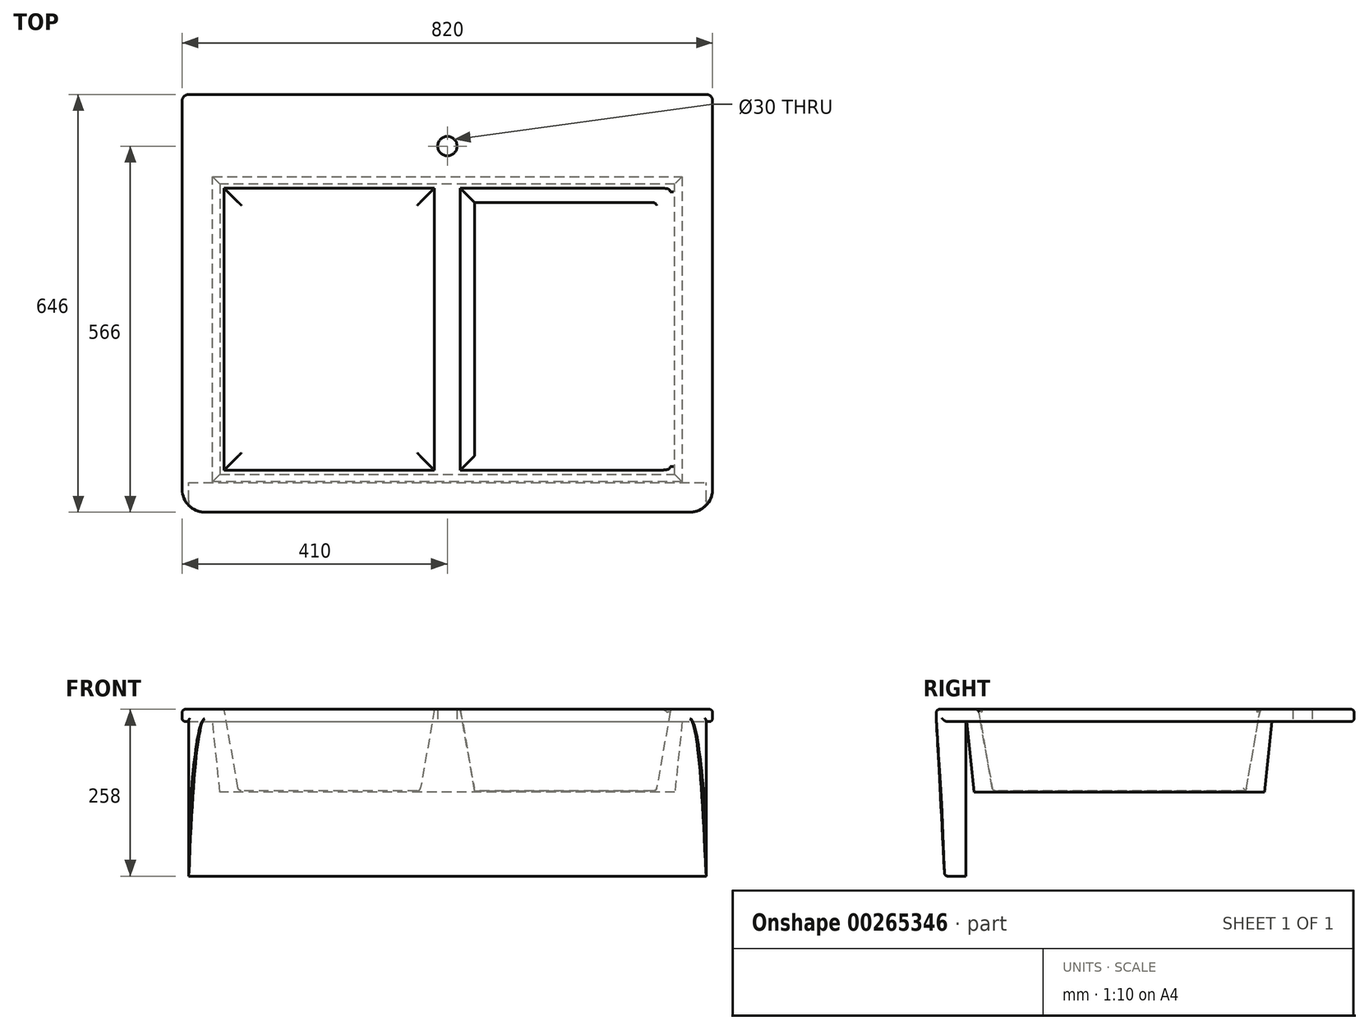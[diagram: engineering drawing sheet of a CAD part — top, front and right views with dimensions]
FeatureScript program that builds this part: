
annotation { "Feature Type Name" : "Feature", "Feature Type Description" : "" }
export const myFeature = defineFeature(function(context is Context, id is Id, definition is map)
    precondition{}
    {
        {
            var Q0;
            Q0=qCreatedBy(makeId("Top.planeOp"),FACE);
            var sketch = newSketch(context, id + "F0", { "sketchPlane" : qUnion([Q0])});
            skLineSegment(sketch, "E0.bottom", {"start": v(-400, 323) * mm, "end": v(400, 323) * mm});
            skLineSegment(sketch, "E0.top", {"start": v(-375, -323) * mm, "end": v(375, -323) * mm});
            skLineSegment(sketch, "E0.left", {"start": v(-410, 313) * mm, "end": v(-410, -288) * mm});
            skLineSegment(sketch, "E0.right", {"start": v(410, 313) * mm, "end": v(410, -288) * mm});
            skPoint(sketch, "E0.middle", {"position": v(0, 0) * mm});
            skPoint(sketch, "E1.visualSharp", {"position": v(-410, 323) * mm});
            skArc(sketch, "E1.filletArc", {"start": v(-400, 323) * mm, "mid": v(-407.07, 320.07) * mm, "end": v(-410, 313) * mm});
            skPoint(sketch, "E2.MirrorP", {"position": v(0, 646) * mm});
            skArc(sketch, "E3.MirrorCS", {"start": v(400, 323) * mm, "mid": v(407.07, 320.07) * mm, "end": v(410, 313) * mm});
            skPoint(sketch, "E4.orphan", {"position": v(410, 323) * mm});
            skPoint(sketch, "E5.visualSharp", {"position": v(410, -323) * mm});
            skArc(sketch, "E5.filletArc", {"start": v(375, -323) * mm, "mid": v(399.75, -312.75) * mm, "end": v(410, -288) * mm});
            skArc(sketch, "E6.MirrorCS", {"start": v(-375, -323) * mm, "mid": v(-399.75, -312.75) * mm, "end": v(-410, -288) * mm});
            skPoint(sketch, "E7.orphan", {"position": v(-410, -323) * mm});
            skLineSegment(sketch, "E8.bottom", {"start": v(20, -258) * mm, "end": v(345, -258) * mm});
            skLineSegment(sketch, "E8.top", {"start": v(20, 178) * mm, "end": v(345, 178) * mm});
            skLineSegment(sketch, "E8.left", {"start": v(20, -258) * mm, "end": v(20, 178) * mm});
            skLineSegment(sketch, "E8.right", {"start": v(345, -258) * mm, "end": v(345, 178) * mm});
            skPoint(sketch, "E8.middle", {"position": v(182.5, -40) * mm});
            skLineSegment(sketch, "E9.MirrorCS", {"start": v(-20, -258) * mm, "end": v(-345, -258) * mm});
            skLineSegment(sketch, "E10.MirrorCS", {"start": v(-20, 178) * mm, "end": v(-345, 178) * mm});
            skLineSegment(sketch, "E11.MirrorCS", {"start": v(-20, -258) * mm, "end": v(-20, 178) * mm});
            skLineSegment(sketch, "E12.MirrorCS", {"start": v(-345, -258) * mm, "end": v(-345, 178) * mm});
            skCircle(sketch, "E13", {"center": v(0, 243) * mm, "radius": 15 * mm});
            skLineSegment(sketch, "E14.0", {"start": v(0, 198) * mm, "end": v(-365, 198) * mm});
            skLineSegment(sketch, "E14.1", {"start": v(0, -278) * mm, "end": v(0, 198) * mm});
            skLineSegment(sketch, "E14.2", {"start": v(0, -278) * mm, "end": v(-365, -278) * mm});
            skLineSegment(sketch, "E14.3", {"start": v(-365, -278) * mm, "end": v(-365, 198) * mm});
            skLineSegment(sketch, "E15.MirrorCS", {"start": v(0, -278) * mm, "end": v(365, -278) * mm});
            skLineSegment(sketch, "E16.MirrorCS", {"start": v(0, 198) * mm, "end": v(365, 198) * mm});
            skLineSegment(sketch, "E17.MirrorCS", {"start": v(365, -278) * mm, "end": v(365, 198) * mm});
            skSolve(sketch);
        }
        {
            var Q0;
            Q0=makeQuery(id+"F0.imprint","IMPRINT",FACE,{"disambiguationData":[TD([[makeQuery(id+"F0.imprint","IMPRINT",EDGE,{"derivedFrom":sQuery(id+"F0.wireOp",EDGE,"E9.MirrorCS")}),-1.0]])]});
            var Q1;
            Q1=makeQuery(id+"F0.imprint","IMPRINT",FACE,{"disambiguationData":[TD([[makeQuery(id+"F0.imprint","IMPRINT",EDGE,{"derivedFrom":sQuery(id+"F0.wireOp",EDGE,"E13")}),1.0]])]});
            var Q2;
            Q2=makeQuery(id+"F0.imprint","IMPRINT",FACE,{"disambiguationData":[TD([[makeQuery(id+"F0.imprint","IMPRINT",EDGE,{"derivedFrom":sQuery(id+"F0.wireOp",EDGE,"E8.bottom")}),1.0]])]});
            var Q3;
            Q3=makeQuery(id+"F0.imprint","IMPRINT",FACE,{"disambiguationData":[TD([[makeQuery(id+"F0.imprint","IMPRINT",EDGE,{"derivedFrom":sQuery(id+"F0.wireOp",EDGE,"E9.MirrorCS")}),1.0]])]});
            var Q4;
            Q4=makeQuery(id+"F0.imprint","IMPRINT",FACE,{"disambiguationData":[TD([[makeQuery(id+"F0.imprint","IMPRINT",EDGE,{"derivedFrom":sQuery(id+"F0.wireOp",EDGE,"E8.bottom")}),-1.0]])]});
            var Q5;
            Q5=makeQuery(id+"F0.imprint","IMPRINT",FACE,{"disambiguationData":[TD([[makeQuery(id+"F0.imprint","IMPRINT",EDGE,{"derivedFrom":sQuery(id+"F0.wireOp",EDGE,"E0.bottom")}),-1.0]])]});
            extrude(context, id + "F1", {"entities" : qUnion([Q0, Q1, Q2, Q3, Q4, Q5]), "oppositeDirection" : true, "depth" : 258 * mm});
        }
        {
            var Q0;
            Q0=makeQuery(id+"F1.opExtrude","SWEPT_FACE",FACE,{"disambiguationData":[OSD([sQuery(id+"F0.wireOp",EDGE,"E0.right")])]});
            var sketch = newSketch(context, id + "F2", { "sketchPlane" : qUnion([Q0])});
            skLineSegment(sketch, "E18.bottom", {"start": v(-277, -258) * mm, "end": v(323, -258) * mm});
            skLineSegment(sketch, "E18.top", {"start": v(-277, -19) * mm, "end": v(323, -19) * mm});
            skLineSegment(sketch, "E18.left", {"start": v(-277, -258) * mm, "end": v(-277, -19) * mm});
            skLineSegment(sketch, "E18.right", {"start": v(323, -258) * mm, "end": v(323, -19) * mm});
            skSolve(sketch);
        }
        {
            var Q0;
            Q0 = qSketchRegion(id + "F2", true);
            extrude(context, id + "F3", {"entities" : qUnion([Q0]), "operationType" : NewBodyOperationType.REMOVE, "oppositeDirection" : true, "depth" : 820 * mm});
        }
        {
            var Q0;
            Q0=makeQuery(id+"F0.imprint","IMPRINT",FACE,{"disambiguationData":[TD([[makeQuery(id+"F0.imprint","IMPRINT",EDGE,{"derivedFrom":sQuery(id+"F0.wireOp",EDGE,"E8.bottom")}),-1.0]])]});
            var Q1;
            Q1=makeQuery(id+"F0.imprint","IMPRINT",FACE,{"disambiguationData":[TD([[makeQuery(id+"F0.imprint","IMPRINT",EDGE,{"derivedFrom":sQuery(id+"F0.wireOp",EDGE,"E9.MirrorCS")}),1.0]])]});
            var Q2;
            Q2=makeQuery(id+"F0.imprint","IMPRINT",FACE,{"disambiguationData":[TD([[makeQuery(id+"F0.imprint","IMPRINT",EDGE,{"derivedFrom":sQuery(id+"F0.wireOp",EDGE,"E8.bottom")}),1.0]])]});
            var Q3;
            Q3=makeQuery(id+"F0.imprint","IMPRINT",FACE,{"disambiguationData":[TD([[makeQuery(id+"F0.imprint","IMPRINT",EDGE,{"derivedFrom":sQuery(id+"F0.wireOp",EDGE,"E9.MirrorCS")}),-1.0]])]});
            extrude(context, id + "F4", {"entities" : qUnion([Q0, Q1, Q2, Q3]), "operationType" : NewBodyOperationType.ADD, "oppositeDirection" : true, "depth" : 128 * mm, "hasDraft" : true, "draftAngle" : 6 * degree, "draftPullDirection" : true});
        }
        {
            var Q0;
            Q0=makeQuery(id+"F0.imprint","IMPRINT",FACE,{"disambiguationData":[TD([[makeQuery(id+"F0.imprint","IMPRINT",EDGE,{"derivedFrom":sQuery(id+"F0.wireOp",EDGE,"E8.bottom")}),1.0]])]});
            var Q1;
            Q1=makeQuery(id+"F0.imprint","IMPRINT",FACE,{"disambiguationData":[TD([[makeQuery(id+"F0.imprint","IMPRINT",EDGE,{"derivedFrom":sQuery(id+"F0.wireOp",EDGE,"E9.MirrorCS")}),-1.0]])]});
            extrude(context, id + "F5", {"entities" : qUnion([Q0, Q1]), "operationType" : NewBodyOperationType.REMOVE, "oppositeDirection" : true, "depth" : 126 * mm, "hasDraft" : true, "draftAngle" : 10 * degree, "draftPullDirection" : true});
        }
        {
            var Q0;
            Q0=sQuery(id+"F0.wireOp",VERTEX,"E13.center");
            var Q1;
            Q1=makeQuery(id+"F1.opExtrude","SWEPT_BODY",BODY,{"disambiguationData":[OSD([sQuery(id+"F0.wireOp",EDGE,"E0.bottom"),sQuery(id+"F0.wireOp",EDGE,"E0.top"),sQuery(id+"F0.wireOp",EDGE,"E0.left"),sQuery(id+"F0.wireOp",EDGE,"E0.right"),sQuery(id+"F0.wireOp",EDGE,"E1.filletArc"),sQuery(id+"F0.wireOp",EDGE,"E3.MirrorCS"),sQuery(id+"F0.wireOp",EDGE,"E5.filletArc"),sQuery(id+"F0.wireOp",EDGE,"E6.MirrorCS")])]});
            hole(context, id + "F6", {"style" : HoleStyle.SIMPLE, "endStyle" : HoleEndStyle.THROUGH, "holeDiameter" : 30 * mm, "tappedDepth" : 12 * mm, "tapClearance" : 3, "locations" : qUnion([Q0]), "scope" : qUnion([Q1]), "startStyle" : HoleStartStyle.PART});
        }
        {
            var Q0;
            Q0=makeQuery(id+"F1.opExtrude","SWEPT_FACE",FACE,{"disambiguationData":[OSD([sQuery(id+"F0.wireOp",EDGE,"E0.right")])]});
            var sketch = newSketch(context, id + "F7", { "sketchPlane" : qUnion([Q0])});
            skLineSegment(sketch, "E19", {"start": v(-323.78, 0) * mm, "end": v(-309.6, -267.77) * mm});
            skLineSegment(sketch, "E20", {"start": v(-309.6, -267.77) * mm, "end": v(-332.86, -267.77) * mm});
            skLineSegment(sketch, "E21", {"start": v(-332.86, -267.77) * mm, "end": v(-323.78, 0) * mm});
            skSolve(sketch);
        }
        {
            var Q0;
            Q0 = qSketchRegion(id + "F7", true);
            extrude(context, id + "F8", {"entities" : qUnion([Q0]), "operationType" : NewBodyOperationType.REMOVE, "oppositeDirection" : true, "depth" : 820 * mm});
        }
        {
            var Q0;
            Q0=makeQuery(id+"F1.opExtrude","CAP_EDGE",EDGE,{"disambiguationData":[OSD([sQuery(id+"F0.wireOp",EDGE,"E0.top")])],"isStart":true});
            var Q1;
            Q1=makeQuery(id+"F5.boolean.opBoolean","COPY",EDGE,{"derivedFrom":makeQuery(id+"F5.opExtrude","CAP_EDGE",EDGE,{"disambiguationData":[OSD([sQuery(id+"F0.wireOp",EDGE,"E10.MirrorCS")])],"isStart":true})});
            var Q2;
            Q2=makeQuery(id+"F5.boolean.opBoolean","COPY",EDGE,{"derivedFrom":makeQuery(id+"F5.opExtrude","CAP_EDGE",EDGE,{"disambiguationData":[OSD([sQuery(id+"F0.wireOp",EDGE,"E12.MirrorCS")])],"isStart":true})});
            var Q3;
            Q3=makeQuery(id+"F5.boolean.opBoolean","COPY",EDGE,{"derivedFrom":makeQuery(id+"F5.opExtrude","CAP_EDGE",EDGE,{"disambiguationData":[OSD([sQuery(id+"F0.wireOp",EDGE,"E9.MirrorCS")])],"isStart":true})});
            var Q4;
            Q4=makeQuery(id+"F5.boolean.opBoolean","COPY",EDGE,{"derivedFrom":makeQuery(id+"F5.opExtrude","CAP_EDGE",EDGE,{"disambiguationData":[OSD([sQuery(id+"F0.wireOp",EDGE,"E11.MirrorCS")])],"isStart":true})});
            var Q5;
            Q5=makeQuery(id+"F5.boolean.opBoolean","COPY",EDGE,{"derivedFrom":makeQuery(id+"F5.opExtrude","CAP_EDGE",EDGE,{"disambiguationData":[OSD([sQuery(id+"F0.wireOp",EDGE,"E11.MirrorCS")])],"isStart":false})});
            var Q6;
            Q6=makeQuery(id+"F5.boolean.opBoolean","COPY",EDGE,{"derivedFrom":makeQuery(id+"F5.opExtrude","CAP_EDGE",EDGE,{"disambiguationData":[OSD([sQuery(id+"F0.wireOp",EDGE,"E9.MirrorCS")])],"isStart":false})});
            var Q7;
            Q7=makeQuery(id+"F5.boolean.opBoolean","COPY",EDGE,{"derivedFrom":makeQuery(id+"F5.opExtrude","CAP_EDGE",EDGE,{"disambiguationData":[OSD([sQuery(id+"F0.wireOp",EDGE,"E12.MirrorCS")])],"isStart":false})});
            var Q8;
            Q8=makeQuery(id+"F5.boolean.opBoolean","COPY",EDGE,{"derivedFrom":makeQuery(id+"F5.opExtrude","CAP_EDGE",EDGE,{"disambiguationData":[OSD([sQuery(id+"F0.wireOp",EDGE,"E10.MirrorCS")])],"isStart":false})});
            var Q9;
            Q9=makeQuery(id+"F5.boolean.opBoolean","COPY",EDGE,{"derivedFrom":makeQuery(id+"F5.opExtrude","CAP_EDGE",EDGE,{"disambiguationData":[OSD([sQuery(id+"F0.wireOp",EDGE,"E8.top")])],"isStart":true})});
            var Q10;
            Q10=makeQuery(id+"F5.boolean.opBoolean","COPY",EDGE,{"derivedFrom":makeQuery(id+"F5.opExtrude","CAP_EDGE",EDGE,{"disambiguationData":[OSD([sQuery(id+"F0.wireOp",EDGE,"E8.left")])],"isStart":true})});
            var Q11;
            Q11=makeQuery(id+"F5.boolean.opBoolean","COPY",FACE,{"derivedFrom":makeQuery(id+"F5.opExtrude","SWEPT_FACE",FACE,{"disambiguationData":[OSD([sQuery(id+"F0.wireOp",EDGE,"E8.right")])]})});
            var Q12;
            Q12=makeQuery(id+"F5.boolean.opBoolean","COPY",EDGE,{"derivedFrom":makeQuery(id+"F5.opExtrude","CAP_EDGE",EDGE,{"disambiguationData":[OSD([sQuery(id+"F0.wireOp",EDGE,"E8.right")])],"isStart":false})});
            var Q13;
            Q13=makeQuery(id+"F5.boolean.opBoolean","COPY",EDGE,{"derivedFrom":makeQuery(id+"F5.opExtrude","CAP_EDGE",EDGE,{"disambiguationData":[OSD([sQuery(id+"F0.wireOp",EDGE,"E8.right")])],"isStart":true})});
            var Q14;
            Q14=makeQuery(id+"F5.boolean.opBoolean","COPY",EDGE,{"derivedFrom":makeQuery(id+"F5.opExtrude","CAP_EDGE",EDGE,{"disambiguationData":[OSD([sQuery(id+"F0.wireOp",EDGE,"E8.bottom")])],"isStart":false})});
            var Q15;
            Q15=makeQuery(id+"F8.boolean.opBoolean","INTERSECT",EDGE,{"derivedFrom":[makeQuery(id+"F1.opExtrude","CAP_FACE",FACE,{"disambiguationData":[OSD([sQuery(id+"F0.wireOp",EDGE,"E0.bottom"),sQuery(id+"F0.wireOp",EDGE,"E0.top"),sQuery(id+"F0.wireOp",EDGE,"E0.left"),sQuery(id+"F0.wireOp",EDGE,"E0.right"),sQuery(id+"F0.wireOp",EDGE,"E1.filletArc"),sQuery(id+"F0.wireOp",EDGE,"E3.MirrorCS"),sQuery(id+"F0.wireOp",EDGE,"E5.filletArc"),sQuery(id+"F0.wireOp",EDGE,"E6.MirrorCS")])],"isStart":false}),makeQuery(id+"F8.opExtrude","SWEPT_FACE",FACE,{"disambiguationData":[OSD([sQuery(id+"F7.wireOp",EDGE,"E19")])]})]});
            var Q16;
            Q16=makeQuery(id+"F1.opExtrude","CAP_EDGE",EDGE,{"disambiguationData":[OSD([sQuery(id+"F0.wireOp",EDGE,"E5.filletArc")])],"isStart":false});
            var Q17;
            Q17=makeQuery(id+"F1.opExtrude","CAP_EDGE",EDGE,{"disambiguationData":[OSD([sQuery(id+"F0.wireOp",EDGE,"E0.right")])],"isStart":false});
            var Q18;
            Q18=makeQuery(id+"F3.boolean.opBoolean","COPY",EDGE,{"derivedFrom":makeQuery(id+"F3.opExtrude","CAP_EDGE",EDGE,{"disambiguationData":[OSD([sQuery(id+"F2.wireOp",EDGE,"E18.left")])],"isStart":true})});
            var Q19;
            Q19=makeQuery(id+"F3.boolean.opBoolean","COPY",EDGE,{"derivedFrom":makeQuery(id+"F3.opExtrude","CAP_EDGE",EDGE,{"disambiguationData":[OSD([sQuery(id+"F2.wireOp",EDGE,"E18.left")])],"isStart":false})});
            fillet(context, id + "F9", {"entities" : qUnion([Q0, Q1, Q2, Q3, Q4, Q5, Q6, Q7, Q8, Q9, Q10, Q11, Q12, Q13, Q14, Q15, Q16, Q17, Q18, Q19]), "radius" : 5 * mm, "tangentPropagation" : true, "allowEdgeOverflow" : false});
        }
        {
            var Q0;
            Q0=makeQuery(id+"F3.boolean.opBoolean","COPY",FACE,{"derivedFrom":makeQuery(id+"F3.opExtrude","SWEPT_FACE",FACE,{"disambiguationData":[OSD([sQuery(id+"F2.wireOp",EDGE,"E18.left")])]})});
            var sketch = newSketch(context, id + "F10", { "sketchPlane" : qUnion([Q0])});
            skLineSegment(sketch, "E22.bottom", {"start": v(-400, -258) * mm, "end": v(-422.11, -258) * mm});
            skLineSegment(sketch, "E22.top", {"start": v(-400, -19) * mm, "end": v(-422.11, -19) * mm});
            skLineSegment(sketch, "E22.left", {"start": v(-400, -258) * mm, "end": v(-400, -19) * mm});
            skLineSegment(sketch, "E22.right", {"start": v(-422.11, -258) * mm, "end": v(-422.11, -19) * mm});
            skLineSegment(sketch, "E23.MirrorCS", {"start": v(400, -258) * mm, "end": v(400, -19) * mm});
            skLineSegment(sketch, "E24.MirrorCS", {"start": v(422.11, -258) * mm, "end": v(422.11, -19) * mm});
            skLineSegment(sketch, "E25.MirrorCS", {"start": v(400, -19) * mm, "end": v(422.11, -19) * mm});
            skLineSegment(sketch, "E26.MirrorCS", {"start": v(400, -258) * mm, "end": v(422.11, -258) * mm});
            skSolve(sketch);
        }
        {
            var Q0;
            Q0 = qSketchRegion(id + "F10", true);
            extrude(context, id + "F11", {"entities" : qUnion([Q0]), "operationType" : NewBodyOperationType.REMOVE, "oppositeDirection" : true, "depth" : 114 * mm});
        }
        {
            var Q0;
            Q0=makeQuery(id+"F11.boolean.opBoolean","INTERSECT",EDGE,{"derivedFrom":[makeQuery(id+"F1.opExtrude","SWEPT_FACE",FACE,{"disambiguationData":[OSD([sQuery(id+"F0.wireOp",EDGE,"E0.right")])]}),makeQuery(id+"F11.opExtrude","SWEPT_FACE",FACE,{"disambiguationData":[OSD([sQuery(id+"F10.wireOp",EDGE,"E22.top")])]})]});
            var Q1;
            Q1=makeQuery(id+"F11.boolean.opBoolean","INTERSECT",EDGE,{"derivedFrom":[makeQuery(id+"F1.opExtrude","SWEPT_FACE",FACE,{"disambiguationData":[OSD([sQuery(id+"F0.wireOp",EDGE,"E5.filletArc")])]}),makeQuery(id+"F11.opExtrude","SWEPT_FACE",FACE,{"disambiguationData":[OSD([sQuery(id+"F10.wireOp",EDGE,"E22.top")])]})]});
            var Q2;
            Q2=makeQuery(id+"F11.boolean.opBoolean","INTERSECT",EDGE,{"derivedFrom":[makeQuery(id+"F1.opExtrude","SWEPT_FACE",FACE,{"disambiguationData":[OSD([sQuery(id+"F0.wireOp",EDGE,"E5.filletArc")])]}),makeQuery(id+"F11.opExtrude","SWEPT_FACE",FACE,{"disambiguationData":[OSD([sQuery(id+"F10.wireOp",EDGE,"E22.left")])]})]});
            var Q3;
            Q3=makeQuery(id+"F11.boolean.opBoolean","COPY",EDGE,{"derivedFrom":makeQuery(id+"F11.opExtrude","CAP_EDGE",EDGE,{"disambiguationData":[OSD([sQuery(id+"F10.wireOp",EDGE,"E22.left")])],"isStart":true})});
            var Q4;
            Q4=makeQuery(id+"F8.boolean.opBoolean","INTERSECT",EDGE,{"derivedFrom":[makeQuery(id+"F1.opExtrude","SWEPT_FACE",FACE,{"disambiguationData":[OSD([sQuery(id+"F0.wireOp",EDGE,"E5.filletArc")])]}),makeQuery(id+"F8.opExtrude","SWEPT_FACE",FACE,{"disambiguationData":[OSD([sQuery(id+"F7.wireOp",EDGE,"E19")])]})]});
            var Q5;
            Q5=makeQuery(id+"F8.boolean.opBoolean","INTERSECT",EDGE,{"derivedFrom":[makeQuery(id+"F1.opExtrude","SWEPT_FACE",FACE,{"disambiguationData":[OSD([sQuery(id+"F0.wireOp",EDGE,"E0.top")])]}),makeQuery(id+"F8.opExtrude","SWEPT_FACE",FACE,{"disambiguationData":[OSD([sQuery(id+"F7.wireOp",EDGE,"E19")])]})]});
            var Q6;
            Q6=makeQuery(id+"F11.boolean.opBoolean","COPY",EDGE,{"derivedFrom":makeQuery(id+"F11.opExtrude","SWEPT_EDGE",EDGE,{"disambiguationData":[OSD([sQuery(id+"F0.wireOp",EDGE,"E0.right"),sQuery(id+"F2.wireOp",EDGE,"E18.bottom"),sQuery(id+"F2.wireOp",EDGE,"E18.left"),sQuery(id+"F10.wireOp",EDGE,"E23.MirrorCS"),sQuery(id+"F10.wireOp",EDGE,"E26.MirrorCS")])]})});
            var Q7;
            Q7=makeQuery(id+"F11.boolean.opBoolean","COPY",EDGE,{"derivedFrom":makeQuery(id+"F11.opExtrude","CAP_EDGE",EDGE,{"disambiguationData":[OSD([sQuery(id+"F10.wireOp",EDGE,"E23.MirrorCS")])],"isStart":true})});
            var Q8;
            Q8=makeQuery(id+"F11.boolean.opBoolean","INTERSECT",EDGE,{"derivedFrom":[makeQuery(id+"F1.opExtrude","SWEPT_FACE",FACE,{"disambiguationData":[OSD([sQuery(id+"F0.wireOp",EDGE,"E6.MirrorCS")])]}),makeQuery(id+"F11.opExtrude","SWEPT_FACE",FACE,{"disambiguationData":[OSD([sQuery(id+"F10.wireOp",EDGE,"E23.MirrorCS")])]})]});
            fillet(context, id + "F12", {"entities" : qUnion([Q0, Q1, Q2, Q3, Q4, Q5, Q6, Q7, Q8]), "radius" : 5 * mm, "tangentPropagation" : true, "allowEdgeOverflow" : false});
        }
    });
